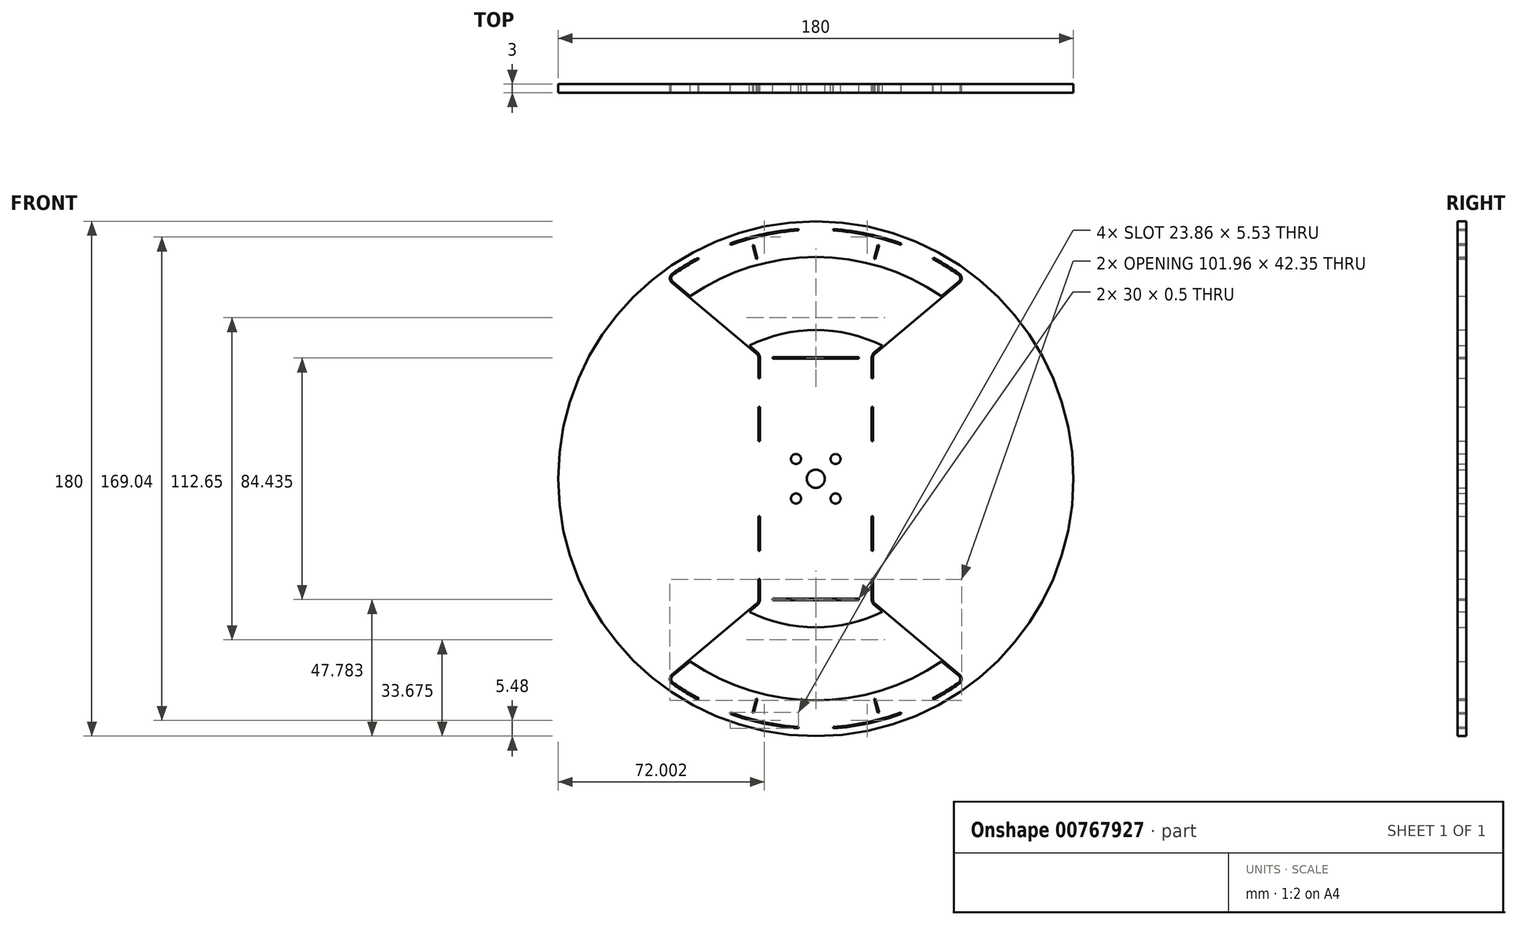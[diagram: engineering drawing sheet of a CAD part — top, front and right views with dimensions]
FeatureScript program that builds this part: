
annotation { "Feature Type Name" : "Feature", "Feature Type Description" : "" }
export const myFeature = defineFeature(function(context is Context, id is Id, definition is map)
    precondition{}
    {
        {
            var Q0;
            Q0=qCreatedBy(makeId("Front.planeOp"),FACE);
            var sketch = newSketch(context, id + "F0", { "sketchPlane" : qUnion([Q0])});
            skCircle(sketch, "E0", {"center": v(0, 0) * mm, "radius": 90 * mm});
            skCircle(sketch, "E1", {"center": v(0, 0) * mm, "radius": 3.17 * mm});
            skCircle(sketch, "E2", {"center": v(6.91, 6.91) * mm, "radius": 1.75 * mm});
            skCircle(sketch, "E3.1.0", {"center": v(6.91, -6.91) * mm, "radius": 1.75 * mm});
            skCircle(sketch, "E3.2.0", {"center": v(-6.91, -6.91) * mm, "radius": 1.75 * mm});
            skCircle(sketch, "E3.3.0", {"center": v(-6.91, 6.91) * mm, "radius": 1.75 * mm});
            skLineSegment(sketch, "E4", {"start": v(0, 0) * mm, "end": v(0, -90) * mm, "construction": true});
            skLineSegment(sketch, "E5", {"start": v(-20, -43.15) * mm, "end": v(20, -43.15) * mm, "construction": true});
            skLineSegment(sketch, "E6", {"start": v(90, 0) * mm, "end": v(-90, 0) * mm, "construction": true});
            skArc(sketch, "E7", {"start": v(-50.13, -71.72) * mm, "mid": v(-45.69, -74.63) * mm, "end": v(-41.08, -77.26) * mm});
            skLineSegment(sketch, "E8", {"start": v(-20.71, -43.75) * mm, "end": v(-23.72, -46.27) * mm});
            skLineSegment(sketch, "E9", {"start": v(-20, -42.22) * mm, "end": v(-20, -35.15) * mm});
            skLineSegment(sketch, "E10", {"start": v(20, -15.15) * mm, "end": v(20, -25.15) * mm});
            skLineSegment(sketch, "E11.MirrorCS", {"start": v(20.71, -43.75) * mm, "end": v(23.72, -46.27) * mm});
            skPoint(sketch, "E12.visualSharp", {"position": v(-52.23, -70.2) * mm});
            skArc(sketch, "E12.filletArc", {"start": v(-50.27, -68.55) * mm, "mid": v(-50.98, -70.17) * mm, "end": v(-50.13, -71.72) * mm});
            skPoint(sketch, "E13.visualSharp", {"position": v(52.23, -70.2) * mm});
            skArc(sketch, "E13.filletArc", {"start": v(50.13, -71.72) * mm, "mid": v(50.98, -70.17) * mm, "end": v(50.27, -68.55) * mm});
            skPoint(sketch, "E14.visualSharp", {"position": v(-20, -43.15) * mm});
            skArc(sketch, "E14.filletArc", {"start": v(-20.71, -43.75) * mm, "mid": v(-20.19, -43.06) * mm, "end": v(-20, -42.22) * mm});
            skPoint(sketch, "E15.visualSharp", {"position": v(20, -43.15) * mm});
            skArc(sketch, "E15.filletArc", {"start": v(20, -42.22) * mm, "mid": v(20.19, -43.06) * mm, "end": v(20.71, -43.75) * mm});
            skLineSegment(sketch, "E16.0", {"start": v(-19.5, -42.22) * mm, "end": v(-19.5, -35.15) * mm});
            skArc(sketch, "E16.1", {"start": v(-20.4, -44.13) * mm, "mid": v(-19.73, -43.27) * mm, "end": v(-19.5, -42.22) * mm});
            skLineSegment(sketch, "E16.3", {"start": v(-20.4, -44.13) * mm, "end": v(-23.24, -46.52) * mm});
            skLineSegment(sketch, "E16.4", {"start": v(19.5, -15.15) * mm, "end": v(19.5, -25.15) * mm});
            skArc(sketch, "E16.5", {"start": v(19.5, -42.22) * mm, "mid": v(19.73, -43.27) * mm, "end": v(20.4, -44.13) * mm});
            skLineSegment(sketch, "E16.6", {"start": v(20.4, -44.13) * mm, "end": v(23.24, -46.52) * mm});
            skArc(sketch, "E16.7", {"start": v(-49.84, -71.3) * mm, "mid": v(-45.43, -74.2) * mm, "end": v(-40.84, -76.82) * mm});
            skPoint(sketch, "E17.visualSharp", {"position": v(-51.43, -70.17) * mm});
            skArc(sketch, "E17.filletArc", {"start": v(-49.95, -68.93) * mm, "mid": v(-50.48, -70.15) * mm, "end": v(-49.84, -71.3) * mm});
            skPoint(sketch, "E18.visualSharp", {"position": v(51.43, -70.17) * mm});
            skArc(sketch, "E18.filletArc", {"start": v(49.84, -71.3) * mm, "mid": v(50.48, -70.15) * mm, "end": v(49.95, -68.93) * mm});
            skArc(sketch, "E19", {"start": v(-43.9, -63.86) * mm, "mid": v(0, -77.5) * mm, "end": v(43.9, -63.86) * mm});
            skLineSegment(sketch, "E20.1.0", {"start": v(-20.4, -76.94) * mm, "end": v(-21.7, -81.77) * mm});
            skLineSegment(sketch, "E20.1.1", {"start": v(-20.8, -76.84) * mm, "end": v(-22.09, -81.67) * mm});
            skPoint(sketch, "E20.1.2", {"position": v(-21.25, -79.3) * mm});
            skLineSegment(sketch, "E20.1.3", {"start": v(-20.4, -76.94) * mm, "end": v(-20.8, -76.84) * mm});
            skLineSegment(sketch, "E20.1.4", {"start": v(-21.7, -81.77) * mm, "end": v(-22.09, -81.67) * mm});
            skLineSegment(sketch, "E21.MirrorCS", {"start": v(21.7, -81.77) * mm, "end": v(22.09, -81.67) * mm});
            skLineSegment(sketch, "E22.MirrorCS", {"start": v(20.4, -76.94) * mm, "end": v(20.8, -76.84) * mm});
            skPoint(sketch, "E23.MirrorP", {"position": v(21.25, -79.3) * mm});
            skLineSegment(sketch, "E24.MirrorCS", {"start": v(20.8, -76.84) * mm, "end": v(22.09, -81.67) * mm});
            skLineSegment(sketch, "E25.MirrorCS", {"start": v(20.4, -76.94) * mm, "end": v(21.7, -81.77) * mm});
            skArc(sketch, "E26", {"start": v(-23.24, -46.52) * mm, "mid": v(0, -52) * mm, "end": v(23.24, -46.52) * mm});
            skLineSegment(sketch, "E27.trimOffspring", {"start": v(-43.9, -63.86) * mm, "end": v(-49.95, -68.93) * mm});
            skLineSegment(sketch, "E28.trimOffspring", {"start": v(-44.33, -63.57) * mm, "end": v(-50.27, -68.55) * mm});
            skLineSegment(sketch, "E29.trimOffspring", {"start": v(43.9, -63.86) * mm, "end": v(49.95, -68.93) * mm});
            skLineSegment(sketch, "E30.trimOffspring", {"start": v(44.33, -63.57) * mm, "end": v(50.27, -68.55) * mm});
            skLineSegment(sketch, "E31", {"start": v(-44.33, -63.57) * mm, "end": v(-23.72, -46.27) * mm});
            skLineSegment(sketch, "E32", {"start": v(23.72, -46.27) * mm, "end": v(44.33, -63.57) * mm});
            skLineSegment(sketch, "E33", {"start": v(-20, -25.15) * mm, "end": v(-19.5, -25.15) * mm});
            skLineSegment(sketch, "E34", {"start": v(-20, -35.15) * mm, "end": v(-19.5, -35.15) * mm});
            skLineSegment(sketch, "E35.MirrorCS", {"start": v(20, -25.15) * mm, "end": v(19.5, -25.15) * mm});
            skLineSegment(sketch, "E36.MirrorCS", {"start": v(20, -35.15) * mm, "end": v(19.5, -35.15) * mm});
            skLineSegment(sketch, "E37.trimOffspring", {"start": v(-19.5, -25.15) * mm, "end": v(-19.5, -15.15) * mm});
            skLineSegment(sketch, "E38.trimOffspring", {"start": v(-20, -25.15) * mm, "end": v(-20, -15.15) * mm});
            skLineSegment(sketch, "E39.trimOffspring", {"start": v(19.5, -35.15) * mm, "end": v(19.5, -42.22) * mm});
            skLineSegment(sketch, "E40.trimOffspring", {"start": v(20, -35.15) * mm, "end": v(20, -42.22) * mm});
            skLineSegment(sketch, "E41.trimOffspring", {"start": v(-29.76, -81.75) * mm, "end": v(-29.93, -82.22) * mm});
            skLineSegment(sketch, "E42.trimOffspring", {"start": v(-40.84, -76.82) * mm, "end": v(-41.08, -77.26) * mm});
            skLineSegment(sketch, "E43.trimOffspring", {"start": v(-6.07, -86.79) * mm, "end": v(-6.1, -87.29) * mm});
            skLineSegment(sketch, "E44.trimOffspring", {"start": v(6.07, -86.79) * mm, "end": v(6.1, -87.29) * mm});
            skLineSegment(sketch, "E45.MirrorCS", {"start": v(29.76, -81.75) * mm, "end": v(29.93, -82.22) * mm});
            skLineSegment(sketch, "E46.MirrorCS", {"start": v(40.84, -76.82) * mm, "end": v(41.08, -77.26) * mm});
            skArc(sketch, "E47.trimOffspring", {"start": v(-29.76, -81.75) * mm, "mid": v(-18.09, -85.1) * mm, "end": v(-6.07, -86.79) * mm});
            skArc(sketch, "E48.trimOffspring", {"start": v(-29.93, -82.22) * mm, "mid": v(-18.2, -85.59) * mm, "end": v(-6.1, -87.29) * mm});
            skArc(sketch, "E49.trimOffspring", {"start": v(6.07, -86.79) * mm, "mid": v(18.09, -85.1) * mm, "end": v(29.76, -81.75) * mm});
            skArc(sketch, "E50.trimOffspring", {"start": v(6.1, -87.29) * mm, "mid": v(18.2, -85.59) * mm, "end": v(29.93, -82.22) * mm});
            skArc(sketch, "E51.trimOffspring", {"start": v(41.08, -77.26) * mm, "mid": v(45.69, -74.63) * mm, "end": v(50.13, -71.72) * mm});
            skArc(sketch, "E52.trimOffspring", {"start": v(40.84, -76.82) * mm, "mid": v(45.43, -74.2) * mm, "end": v(49.84, -71.3) * mm});
            skLineSegment(sketch, "E53", {"start": v(-20, -15.15) * mm, "end": v(-20, -13.15) * mm});
            skLineSegment(sketch, "E54", {"start": v(-19.5, -15.15) * mm, "end": v(-19.5, -13.15) * mm});
            skLineSegment(sketch, "E55", {"start": v(-19.5, -13.15) * mm, "end": v(-20, -13.15) * mm});
            skLineSegment(sketch, "E56", {"start": v(20, -15.15) * mm, "end": v(20, -13.15) * mm});
            skLineSegment(sketch, "E57", {"start": v(20, -13.15) * mm, "end": v(19.5, -13.15) * mm});
            skLineSegment(sketch, "E58", {"start": v(19.5, -13.15) * mm, "end": v(19.5, -15.15) * mm});
            skArc(sketch, "E59.MirrorCS", {"start": v(20, 42.22) * mm, "mid": v(20.19, 43.06) * mm, "end": v(20.71, 43.75) * mm});
            skLineSegment(sketch, "E60.MirrorCS", {"start": v(-20.4, 44.13) * mm, "end": v(-23.24, 46.52) * mm});
            skLineSegment(sketch, "E61.MirrorCS", {"start": v(20.4, 44.13) * mm, "end": v(23.24, 46.52) * mm});
            skArc(sketch, "E62.MirrorCS", {"start": v(-20.71, 43.75) * mm, "mid": v(-20.19, 43.06) * mm, "end": v(-20, 42.22) * mm});
            skArc(sketch, "E63.MirrorCS", {"start": v(-20.4, 44.13) * mm, "mid": v(-19.73, 43.27) * mm, "end": v(-19.5, 42.22) * mm});
            skArc(sketch, "E64.MirrorCS", {"start": v(19.5, 42.22) * mm, "mid": v(19.73, 43.27) * mm, "end": v(20.4, 44.13) * mm});
            skArc(sketch, "E65.MirrorCS", {"start": v(50.13, 71.72) * mm, "mid": v(50.98, 70.17) * mm, "end": v(50.27, 68.55) * mm});
            skLineSegment(sketch, "E66.MirrorCS", {"start": v(20.4, 76.94) * mm, "end": v(20.8, 76.84) * mm});
            skLineSegment(sketch, "E67.MirrorCS", {"start": v(-20.4, 76.94) * mm, "end": v(-20.8, 76.84) * mm});
            skLineSegment(sketch, "E68.MirrorCS", {"start": v(-43.9, 63.86) * mm, "end": v(-49.95, 68.93) * mm});
            skLineSegment(sketch, "E69.MirrorCS", {"start": v(21.7, 81.77) * mm, "end": v(22.09, 81.67) * mm});
            skLineSegment(sketch, "E70.MirrorCS", {"start": v(-20.71, 43.75) * mm, "end": v(-23.72, 46.27) * mm});
            skArc(sketch, "E71.MirrorCS", {"start": v(-50.27, 68.55) * mm, "mid": v(-50.98, 70.17) * mm, "end": v(-50.13, 71.72) * mm});
            skArc(sketch, "E72.MirrorCS", {"start": v(49.84, 71.3) * mm, "mid": v(50.48, 70.15) * mm, "end": v(49.95, 68.93) * mm});
            skLineSegment(sketch, "E73.MirrorCS", {"start": v(20.71, 43.75) * mm, "end": v(23.72, 46.27) * mm});
            skLineSegment(sketch, "E74.MirrorCS", {"start": v(-21.7, 81.77) * mm, "end": v(-22.09, 81.67) * mm});
            skArc(sketch, "E75.MirrorCS", {"start": v(-49.95, 68.93) * mm, "mid": v(-50.48, 70.15) * mm, "end": v(-49.84, 71.3) * mm});
            skLineSegment(sketch, "E76.MirrorCS", {"start": v(20, 15.15) * mm, "end": v(20, 13.15) * mm});
            skLineSegment(sketch, "E77.MirrorCS", {"start": v(20.4, 76.94) * mm, "end": v(21.7, 81.77) * mm});
            skLineSegment(sketch, "E78.MirrorCS", {"start": v(-20.4, 76.94) * mm, "end": v(-21.7, 81.77) * mm});
            skLineSegment(sketch, "E79.MirrorCS", {"start": v(20, 13.15) * mm, "end": v(19.5, 13.15) * mm});
            skLineSegment(sketch, "E80.MirrorCS", {"start": v(19.5, 13.15) * mm, "end": v(19.5, 15.15) * mm});
            skLineSegment(sketch, "E81.MirrorCS", {"start": v(-20.8, 76.84) * mm, "end": v(-22.09, 81.67) * mm});
            skLineSegment(sketch, "E82.MirrorCS", {"start": v(43.9, 63.86) * mm, "end": v(49.95, 68.93) * mm});
            skLineSegment(sketch, "E83.MirrorCS", {"start": v(40.84, 76.82) * mm, "end": v(41.08, 77.26) * mm});
            skLineSegment(sketch, "E84.MirrorCS", {"start": v(20.8, 76.84) * mm, "end": v(22.09, 81.67) * mm});
            skLineSegment(sketch, "E85.MirrorCS", {"start": v(29.76, 81.75) * mm, "end": v(29.93, 82.22) * mm});
            skLineSegment(sketch, "E86.MirrorCS", {"start": v(-19.5, 15.15) * mm, "end": v(-19.5, 13.15) * mm});
            skLineSegment(sketch, "E87.MirrorCS", {"start": v(-20, 35.15) * mm, "end": v(-19.5, 35.15) * mm});
            skLineSegment(sketch, "E88.MirrorCS", {"start": v(-40.84, 76.82) * mm, "end": v(-41.08, 77.26) * mm});
            skLineSegment(sketch, "E89.MirrorCS", {"start": v(20, 35.15) * mm, "end": v(19.5, 35.15) * mm});
            skLineSegment(sketch, "E90.MirrorCS", {"start": v(-6.07, 86.79) * mm, "end": v(-6.1, 87.29) * mm});
            skLineSegment(sketch, "E91.MirrorCS", {"start": v(20, 25.15) * mm, "end": v(19.5, 25.15) * mm});
            skLineSegment(sketch, "E92.MirrorCS", {"start": v(-20, 25.15) * mm, "end": v(-19.5, 25.15) * mm});
            skLineSegment(sketch, "E93.MirrorCS", {"start": v(-29.76, 81.75) * mm, "end": v(-29.93, 82.22) * mm});
            skLineSegment(sketch, "E94.MirrorCS", {"start": v(-20, 15.15) * mm, "end": v(-20, 13.15) * mm});
            skLineSegment(sketch, "E95.MirrorCS", {"start": v(6.07, 86.79) * mm, "end": v(6.1, 87.29) * mm});
            skLineSegment(sketch, "E96.MirrorCS", {"start": v(-19.5, 13.15) * mm, "end": v(-20, 13.15) * mm});
            skLineSegment(sketch, "E97.MirrorCS", {"start": v(-20, 25.15) * mm, "end": v(-20, 15.15) * mm});
            skArc(sketch, "E98.MirrorCS", {"start": v(-49.84, 71.3) * mm, "mid": v(-45.43, 74.2) * mm, "end": v(-40.84, 76.82) * mm});
            skPoint(sketch, "E99.MirrorP", {"position": v(51.43, 70.17) * mm});
            skPoint(sketch, "E100.MirrorP", {"position": v(-51.43, 70.17) * mm});
            skLineSegment(sketch, "E101.MirrorCS", {"start": v(-19.5, 25.15) * mm, "end": v(-19.5, 15.15) * mm});
            skArc(sketch, "E102.MirrorCS", {"start": v(40.84, 76.82) * mm, "mid": v(45.43, 74.2) * mm, "end": v(49.84, 71.3) * mm});
            skLineSegment(sketch, "E103.MirrorCS", {"start": v(19.5, 35.15) * mm, "end": v(19.5, 42.22) * mm});
            skArc(sketch, "E104.MirrorCS", {"start": v(-29.76, 81.75) * mm, "mid": v(-18.09, 85.1) * mm, "end": v(-6.07, 86.79) * mm});
            skLineSegment(sketch, "E105.MirrorCS", {"start": v(-20, 42.22) * mm, "end": v(-20, 35.15) * mm});
            skArc(sketch, "E106.MirrorCS", {"start": v(-29.93, 82.22) * mm, "mid": v(-18.2, 85.59) * mm, "end": v(-6.1, 87.29) * mm});
            skLineSegment(sketch, "E107.MirrorCS", {"start": v(23.72, 46.27) * mm, "end": v(44.33, 63.57) * mm});
            skPoint(sketch, "E108.MirrorP", {"position": v(-52.23, 70.2) * mm});
            skArc(sketch, "E109.MirrorCS", {"start": v(41.08, 77.26) * mm, "mid": v(45.69, 74.63) * mm, "end": v(50.13, 71.72) * mm});
            skArc(sketch, "E110.MirrorCS", {"start": v(-43.9, 63.86) * mm, "mid": v(0, 77.5) * mm, "end": v(43.9, 63.86) * mm});
            skPoint(sketch, "E111.MirrorP", {"position": v(-20, 43.15) * mm});
            skPoint(sketch, "E112.MirrorP", {"position": v(-21.25, 79.3) * mm});
            skPoint(sketch, "E113.MirrorP", {"position": v(20, 43.15) * mm});
            skArc(sketch, "E114.MirrorCS", {"start": v(-23.24, 46.52) * mm, "mid": v(0, 52) * mm, "end": v(23.24, 46.52) * mm});
            skPoint(sketch, "E115.MirrorP", {"position": v(21.25, 79.3) * mm});
            skArc(sketch, "E116.MirrorCS", {"start": v(6.1, 87.29) * mm, "mid": v(18.2, 85.59) * mm, "end": v(29.93, 82.22) * mm});
            skPoint(sketch, "E117.MirrorP", {"position": v(52.23, 70.2) * mm});
            skLineSegment(sketch, "E118.MirrorCS", {"start": v(-44.33, 63.57) * mm, "end": v(-23.72, 46.27) * mm});
            skLineSegment(sketch, "E119.MirrorCS", {"start": v(-20, 43.15) * mm, "end": v(20, 43.15) * mm, "construction": true});
            skArc(sketch, "E120.MirrorCS", {"start": v(-50.13, 71.72) * mm, "mid": v(-45.69, 74.63) * mm, "end": v(-41.08, 77.26) * mm});
            skArc(sketch, "E121.MirrorCS", {"start": v(6.07, 86.79) * mm, "mid": v(18.09, 85.1) * mm, "end": v(29.76, 81.75) * mm});
            skLineSegment(sketch, "E122.MirrorCS", {"start": v(-19.5, 42.22) * mm, "end": v(-19.5, 35.15) * mm});
            skLineSegment(sketch, "E123.MirrorCS", {"start": v(20, 15.15) * mm, "end": v(20, 25.15) * mm});
            skLineSegment(sketch, "E124.MirrorCS", {"start": v(20, 35.15) * mm, "end": v(20, 42.22) * mm});
            skLineSegment(sketch, "E125.MirrorCS", {"start": v(44.33, 63.57) * mm, "end": v(50.27, 68.55) * mm});
            skLineSegment(sketch, "E126.MirrorCS", {"start": v(-44.33, 63.57) * mm, "end": v(-50.27, 68.55) * mm});
            skLineSegment(sketch, "E127.MirrorCS", {"start": v(19.5, 15.15) * mm, "end": v(19.5, 25.15) * mm});
            skLineSegment(sketch, "E128.bottom", {"start": v(15, -41.97) * mm, "end": v(-15, -41.97) * mm});
            skLineSegment(sketch, "E128.top", {"start": v(15, -42.47) * mm, "end": v(-15, -42.47) * mm});
            skLineSegment(sketch, "E128.left", {"start": v(15, -41.97) * mm, "end": v(15, -42.47) * mm});
            skLineSegment(sketch, "E128.right", {"start": v(-15, -41.97) * mm, "end": v(-15, -42.47) * mm});
            skPoint(sketch, "E128.middle", {"position": v(0, -42.22) * mm});
            skLineSegment(sketch, "E129.MirrorCS", {"start": v(15, 41.97) * mm, "end": v(15, 42.47) * mm});
            skLineSegment(sketch, "E130.MirrorCS", {"start": v(-15, 41.97) * mm, "end": v(-15, 42.47) * mm});
            skLineSegment(sketch, "E131.MirrorCS", {"start": v(15, 42.47) * mm, "end": v(-15, 42.47) * mm});
            skPoint(sketch, "E132.MirrorP", {"position": v(0, 42.22) * mm});
            skLineSegment(sketch, "E133.MirrorCS", {"start": v(15, 41.97) * mm, "end": v(-15, 41.97) * mm});
            skSolve(sketch);
        }
        {
            var Q0;
            Q0=makeQuery(id+"F0.imprint","IMPRINT",FACE,{"disambiguationData":[TD([[makeQuery(id+"F0.imprint","IMPRINT",EDGE,{"derivedFrom":sQuery(id+"F0.wireOp",EDGE,"E0")}),1.0]])]});
            extrude(context, id + "F1", {"entities" : qUnion([Q0]), "depth" : 3 * mm, "offsetDistance" : 25 * mm});
        }
    });
